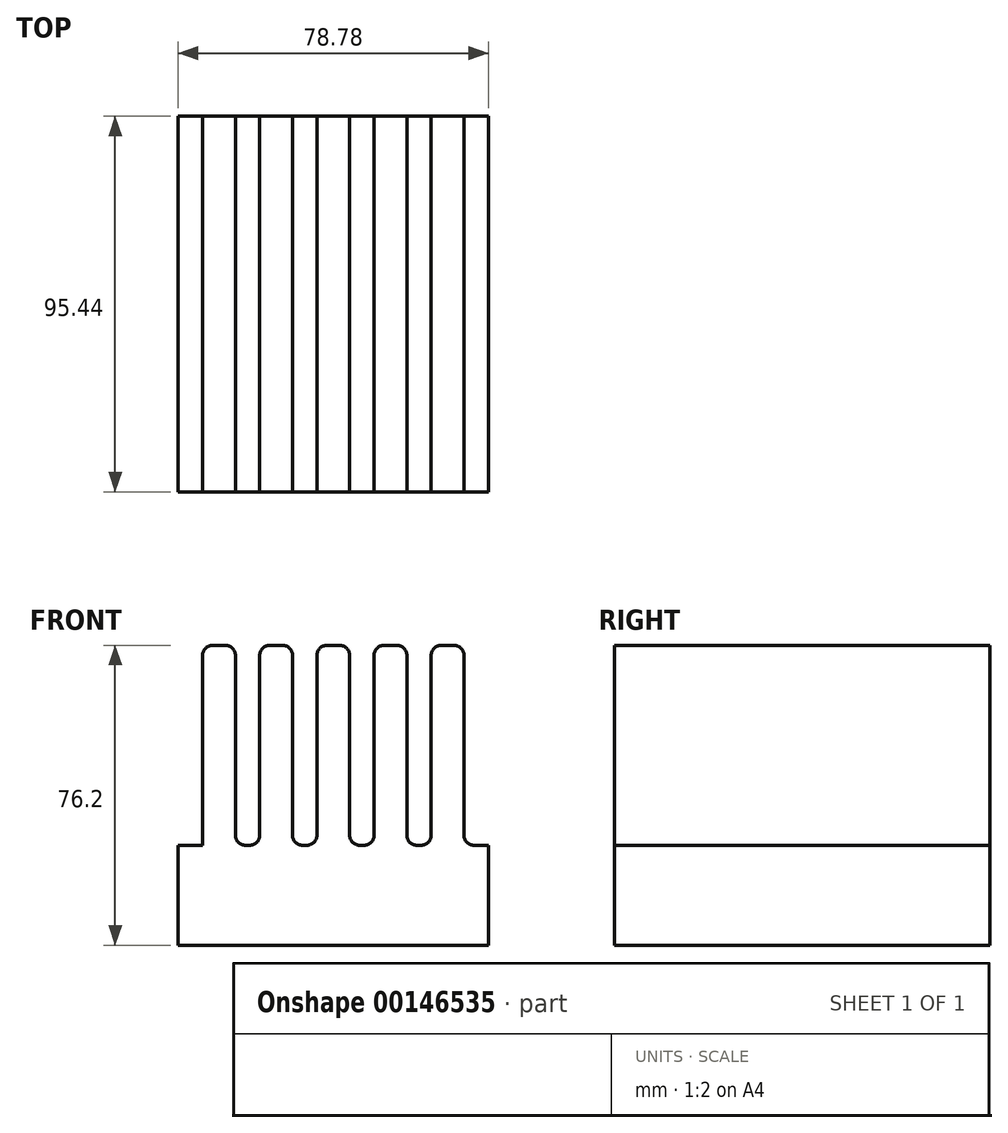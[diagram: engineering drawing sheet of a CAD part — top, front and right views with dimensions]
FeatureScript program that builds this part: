
annotation { "Feature Type Name" : "Feature", "Feature Type Description" : "" }
export const myFeature = defineFeature(function(context is Context, id is Id, definition is map)
    precondition{}
    {
        {
            var Q0;
            Q0=qCreatedBy(makeId("Top.planeOp"),FACE);
            var sketch = newSketch(context, id + "F0", { "sketchPlane" : qUnion([Q0])});
            skLineSegment(sketch, "E0.bottom", {"start": v(47.72, -47.72) * mm, "end": v(-47.72, -47.72) * mm});
            skLineSegment(sketch, "E0.top", {"start": v(47.72, 47.72) * mm, "end": v(-47.72, 47.72) * mm});
            skLineSegment(sketch, "E0.left", {"start": v(47.72, -47.72) * mm, "end": v(47.72, 47.72) * mm});
            skLineSegment(sketch, "E0.right", {"start": v(-47.72, -47.72) * mm, "end": v(-47.72, 47.72) * mm});
            skPoint(sketch, "E0.middle", {"position": v(0, 0) * mm});
            skLineSegment(sketch, "E1.bottom", {"start": v(-47.72, 47.72) * mm, "end": v(-39.39, 47.72) * mm});
            skLineSegment(sketch, "E1.top", {"start": v(-47.72, -47.72) * mm, "end": v(-39.39, -47.72) * mm});
            skLineSegment(sketch, "E1.left", {"start": v(-47.72, 47.72) * mm, "end": v(-47.72, -47.72) * mm});
            skLineSegment(sketch, "E1.right", {"start": v(-39.39, 47.72) * mm, "end": v(-39.39, -47.72) * mm});
            skLineSegment(sketch, "E2.1.0.0", {"start": v(-24.87, 47.72) * mm, "end": v(-24.87, -47.72) * mm});
            skLineSegment(sketch, "E2.1.0.1", {"start": v(-33.2, 47.72) * mm, "end": v(-24.87, 47.72) * mm});
            skLineSegment(sketch, "E2.1.0.2", {"start": v(-33.2, 47.72) * mm, "end": v(-33.2, -47.72) * mm});
            skLineSegment(sketch, "E2.1.0.3", {"start": v(-33.2, -47.72) * mm, "end": v(-24.87, -47.72) * mm});
            skLineSegment(sketch, "E2.2.0.0", {"start": v(-10.35, 47.72) * mm, "end": v(-10.35, -47.72) * mm});
            skLineSegment(sketch, "E2.2.0.1", {"start": v(-18.69, 47.72) * mm, "end": v(-10.35, 47.72) * mm});
            skLineSegment(sketch, "E2.2.0.2", {"start": v(-18.69, 47.72) * mm, "end": v(-18.69, -47.72) * mm});
            skLineSegment(sketch, "E2.2.0.3", {"start": v(-18.69, -47.72) * mm, "end": v(-10.35, -47.72) * mm});
            skLineSegment(sketch, "E2.3.0.0", {"start": v(4.17, 47.72) * mm, "end": v(4.17, -47.72) * mm});
            skLineSegment(sketch, "E2.3.0.1", {"start": v(-4.17, 47.72) * mm, "end": v(4.17, 47.72) * mm});
            skLineSegment(sketch, "E2.3.0.2", {"start": v(-4.17, 47.72) * mm, "end": v(-4.17, -47.72) * mm});
            skLineSegment(sketch, "E2.3.0.3", {"start": v(-4.17, -47.72) * mm, "end": v(4.17, -47.72) * mm});
            skLineSegment(sketch, "E2.4.0.0", {"start": v(18.69, 47.72) * mm, "end": v(18.69, -47.72) * mm});
            skLineSegment(sketch, "E2.4.0.1", {"start": v(10.35, 47.72) * mm, "end": v(18.69, 47.72) * mm});
            skLineSegment(sketch, "E2.4.0.2", {"start": v(10.35, 47.72) * mm, "end": v(10.35, -47.72) * mm});
            skLineSegment(sketch, "E2.4.0.3", {"start": v(10.35, -47.72) * mm, "end": v(18.69, -47.72) * mm});
            skLineSegment(sketch, "E2.5.0.0", {"start": v(33.2, 47.72) * mm, "end": v(33.2, -47.72) * mm});
            skLineSegment(sketch, "E2.5.0.1", {"start": v(24.87, 47.72) * mm, "end": v(33.2, 47.72) * mm});
            skLineSegment(sketch, "E2.5.0.2", {"start": v(24.87, 47.72) * mm, "end": v(24.87, -47.72) * mm});
            skLineSegment(sketch, "E2.5.0.3", {"start": v(24.87, -47.72) * mm, "end": v(33.2, -47.72) * mm});
            skLineSegment(sketch, "E2.6.0.0", {"start": v(47.72, 47.72) * mm, "end": v(47.72, -47.72) * mm});
            skLineSegment(sketch, "E2.6.0.1", {"start": v(39.39, 47.72) * mm, "end": v(47.72, 47.72) * mm});
            skLineSegment(sketch, "E2.6.0.2", {"start": v(39.39, 47.72) * mm, "end": v(39.39, -47.72) * mm});
            skLineSegment(sketch, "E2.6.0.3", {"start": v(39.39, -47.72) * mm, "end": v(47.72, -47.72) * mm});
            skLineSegment(sketch, "E2.direction1", {"start": v(-39.39, -47.72) * mm, "end": v(-24.87, -47.72) * mm, "construction": true});
            skSolve(sketch);
        }
        {
            var Q0;
            Q0=makeQuery(id+"F0.imprint","IMPRINT",FACE,{"disambiguationData":[TD([[makeQuery(id+"F0.imprint","IMPRINT",EDGE,{"derivedFrom":sQuery(id+"F0.wireOp",EDGE,"E1.bottom")}),-1.0]])]});
            var Q1;
            Q1=makeQuery(id+"F0.imprint","IMPRINT",FACE,{"disambiguationData":[TD([[makeQuery(id+"F0.imprint","IMPRINT",EDGE,{"derivedFrom":sQuery(id+"F0.wireOp",EDGE,"E2.6.0.0")}),-1.0]])]});
            var Q2;
            {var subQ2=sQuery(id+"F0.wireOp",EDGE,"E2.5.0.0");Q2=makeQuery(id+"F0.imprint","IMPRINT",FACE,{"disambiguationData":[TD([[makeQuery(id+"F0.imprint","IMPRINT",EDGE,{"derivedFrom":subQ2}),1.0]])]});}
            var Q3;
            {var subQ0=sQuery(id+"F0.wireOp",EDGE,"E2.4.0.0");Q3=makeQuery(id+"F0.imprint","IMPRINT",FACE,{"disambiguationData":[TD([[makeQuery(id+"F0.imprint","IMPRINT",EDGE,{"derivedFrom":subQ0}),1.0]])]});}
            var Q4;
            {var subQ0=sQuery(id+"F0.wireOp",EDGE,"E2.3.0.0");Q4=makeQuery(id+"F0.imprint","IMPRINT",FACE,{"disambiguationData":[TD([[makeQuery(id+"F0.imprint","IMPRINT",EDGE,{"derivedFrom":subQ0}),1.0]])]});}
            var Q5;
            {var subQ0=sQuery(id+"F0.wireOp",EDGE,"E2.2.0.0");Q5=makeQuery(id+"F0.imprint","IMPRINT",FACE,{"disambiguationData":[TD([[makeQuery(id+"F0.imprint","IMPRINT",EDGE,{"derivedFrom":subQ0}),1.0]])]});}
            var Q6;
            {var subQ0=sQuery(id+"F0.wireOp",EDGE,"E2.1.0.0");Q6=makeQuery(id+"F0.imprint","IMPRINT",FACE,{"disambiguationData":[TD([[makeQuery(id+"F0.imprint","IMPRINT",EDGE,{"derivedFrom":subQ0}),1.0]])]});}
            var Q7;
            {var subQ0=sQuery(id+"F0.wireOp",EDGE,"E1.right");Q7=makeQuery(id+"F0.imprint","IMPRINT",FACE,{"disambiguationData":[TD([[makeQuery(id+"F0.imprint","IMPRINT",EDGE,{"derivedFrom":subQ0}),1.0]])]});}
            var Q8;
            Q8=makeQuery(id+"F0.imprint","IMPRINT",FACE,{"disambiguationData":[TD([[makeQuery(id+"F0.imprint","IMPRINT",EDGE,{"derivedFrom":sQuery(id+"F0.wireOp",EDGE,"E2.1.0.0")}),-1.0]])]});
            var Q9;
            Q9=makeQuery(id+"F0.imprint","IMPRINT",FACE,{"disambiguationData":[TD([[makeQuery(id+"F0.imprint","IMPRINT",EDGE,{"derivedFrom":sQuery(id+"F0.wireOp",EDGE,"E2.2.0.0")}),-1.0]])]});
            var Q10;
            Q10=makeQuery(id+"F0.imprint","IMPRINT",FACE,{"disambiguationData":[TD([[makeQuery(id+"F0.imprint","IMPRINT",EDGE,{"derivedFrom":sQuery(id+"F0.wireOp",EDGE,"E2.3.0.0")}),-1.0]])]});
            var Q11;
            Q11=makeQuery(id+"F0.imprint","IMPRINT",FACE,{"disambiguationData":[TD([[makeQuery(id+"F0.imprint","IMPRINT",EDGE,{"derivedFrom":sQuery(id+"F0.wireOp",EDGE,"E2.4.0.0")}),-1.0]])]});
            var Q12;
            Q12=makeQuery(id+"F0.imprint","IMPRINT",FACE,{"disambiguationData":[TD([[makeQuery(id+"F0.imprint","IMPRINT",EDGE,{"derivedFrom":sQuery(id+"F0.wireOp",EDGE,"E2.5.0.0")}),-1.0]])]});
            extrude(context, id + "F1", {"entities" : qUnion([Q0, Q1, Q2, Q3, Q4, Q5, Q6, Q7, Q8, Q9, Q10, Q11, Q12]), "oppositeDirection" : true, "depth" : 25.4 * mm});
        }
        {
            var Q0;
            Q0=makeQuery(id+"F0.imprint","IMPRINT",FACE,{"disambiguationData":[TD([[makeQuery(id+"F0.imprint","IMPRINT",EDGE,{"derivedFrom":sQuery(id+"F0.wireOp",EDGE,"E1.bottom")}),-1.0]])]});
            var Q1;
            Q1=makeQuery(id+"F0.imprint","IMPRINT",FACE,{"disambiguationData":[TD([[makeQuery(id+"F0.imprint","IMPRINT",EDGE,{"derivedFrom":sQuery(id+"F0.wireOp",EDGE,"E2.1.0.0")}),-1.0]])]});
            var Q2;
            Q2=makeQuery(id+"F0.imprint","IMPRINT",FACE,{"disambiguationData":[TD([[makeQuery(id+"F0.imprint","IMPRINT",EDGE,{"derivedFrom":sQuery(id+"F0.wireOp",EDGE,"E2.2.0.0")}),-1.0]])]});
            var Q3;
            Q3=makeQuery(id+"F0.imprint","IMPRINT",FACE,{"disambiguationData":[TD([[makeQuery(id+"F0.imprint","IMPRINT",EDGE,{"derivedFrom":sQuery(id+"F0.wireOp",EDGE,"E2.3.0.0")}),-1.0]])]});
            var Q4;
            Q4=makeQuery(id+"F0.imprint","IMPRINT",FACE,{"disambiguationData":[TD([[makeQuery(id+"F0.imprint","IMPRINT",EDGE,{"derivedFrom":sQuery(id+"F0.wireOp",EDGE,"E2.4.0.0")}),-1.0]])]});
            var Q5;
            Q5=makeQuery(id+"F0.imprint","IMPRINT",FACE,{"disambiguationData":[TD([[makeQuery(id+"F0.imprint","IMPRINT",EDGE,{"derivedFrom":sQuery(id+"F0.wireOp",EDGE,"E2.5.0.0")}),-1.0]])]});
            var Q6;
            Q6=makeQuery(id+"F0.imprint","IMPRINT",FACE,{"disambiguationData":[TD([[makeQuery(id+"F0.imprint","IMPRINT",EDGE,{"derivedFrom":sQuery(id+"F0.wireOp",EDGE,"E2.6.0.0")}),-1.0]])]});
            extrude(context, id + "F2", {"entities" : qUnion([Q0, Q1, Q2, Q3, Q4, Q5, Q6]), "operationType" : NewBodyOperationType.ADD, "depth" : 50.8 * mm});
        }
        {
            var Q0;
            Q0=makeQuery(id+"F2.opExtrude","CAP_EDGE",EDGE,{"disambiguationData":[OSD([sQuery(id+"F0.wireOp",EDGE,"E1.left")])],"isStart":false});
            var Q1;
            Q1=makeQuery(id+"F2.opExtrude","CAP_EDGE",EDGE,{"disambiguationData":[OSD([sQuery(id+"F0.wireOp",EDGE,"E1.right")])],"isStart":false});
            var Q2;
            Q2=makeQuery(id+"F2.opExtrude","CAP_EDGE",EDGE,{"disambiguationData":[OSD([sQuery(id+"F0.wireOp",EDGE,"E2.1.0.2")])],"isStart":false});
            var Q3;
            Q3=makeQuery(id+"F2.opExtrude","CAP_EDGE",EDGE,{"disambiguationData":[OSD([sQuery(id+"F0.wireOp",EDGE,"E2.1.0.0")])],"isStart":false});
            var Q4;
            Q4=makeQuery(id+"F2.opExtrude","CAP_EDGE",EDGE,{"disambiguationData":[OSD([sQuery(id+"F0.wireOp",EDGE,"E2.2.0.2")])],"isStart":false});
            var Q5;
            Q5=makeQuery(id+"F2.opExtrude","CAP_EDGE",EDGE,{"disambiguationData":[OSD([sQuery(id+"F0.wireOp",EDGE,"E2.2.0.0")])],"isStart":false});
            var Q6;
            Q6=makeQuery(id+"F2.opExtrude","CAP_EDGE",EDGE,{"disambiguationData":[OSD([sQuery(id+"F0.wireOp",EDGE,"E2.3.0.2")])],"isStart":false});
            var Q7;
            Q7=makeQuery(id+"F2.opExtrude","CAP_EDGE",EDGE,{"disambiguationData":[OSD([sQuery(id+"F0.wireOp",EDGE,"E2.3.0.0")])],"isStart":false});
            var Q8;
            Q8=makeQuery(id+"F2.opExtrude","CAP_EDGE",EDGE,{"disambiguationData":[OSD([sQuery(id+"F0.wireOp",EDGE,"E2.4.0.2")])],"isStart":false});
            var Q9;
            Q9=makeQuery(id+"F2.opExtrude","CAP_EDGE",EDGE,{"disambiguationData":[OSD([sQuery(id+"F0.wireOp",EDGE,"E2.4.0.0")])],"isStart":false});
            var Q10;
            Q10=makeQuery(id+"F2.opExtrude","CAP_EDGE",EDGE,{"disambiguationData":[OSD([sQuery(id+"F0.wireOp",EDGE,"E2.5.0.2")])],"isStart":false});
            var Q11;
            Q11=makeQuery(id+"F2.opExtrude","CAP_EDGE",EDGE,{"disambiguationData":[OSD([sQuery(id+"F0.wireOp",EDGE,"E2.5.0.0")])],"isStart":false});
            var Q12;
            Q12=makeQuery(id+"F2.opExtrude","CAP_EDGE",EDGE,{"disambiguationData":[OSD([sQuery(id+"F0.wireOp",EDGE,"E2.6.0.2")])],"isStart":false});
            var Q13;
            Q13=makeQuery(id+"F2.opExtrude","CAP_EDGE",EDGE,{"disambiguationData":[OSD([sQuery(id+"F0.wireOp",EDGE,"E2.6.0.0")])],"isStart":false});
            var Q14;
            Q14=makeQuery(id+"F2.opExtrude","CAP_EDGE",EDGE,{"disambiguationData":[OSD([sQuery(id+"F0.wireOp",EDGE,"E2.5.0.0")])],"isStart":true});
            var Q15;
            Q15=makeQuery(id+"F2.opExtrude","CAP_EDGE",EDGE,{"disambiguationData":[OSD([sQuery(id+"F0.wireOp",EDGE,"E2.4.0.0")])],"isStart":true});
            var Q16;
            Q16=makeQuery(id+"F2.opExtrude","CAP_EDGE",EDGE,{"disambiguationData":[OSD([sQuery(id+"F0.wireOp",EDGE,"E2.3.0.0")])],"isStart":true});
            var Q17;
            Q17=makeQuery(id+"F2.opExtrude","CAP_EDGE",EDGE,{"disambiguationData":[OSD([sQuery(id+"F0.wireOp",EDGE,"E2.2.0.0")])],"isStart":true});
            var Q18;
            Q18=makeQuery(id+"F2.opExtrude","CAP_EDGE",EDGE,{"disambiguationData":[OSD([sQuery(id+"F0.wireOp",EDGE,"E2.1.0.0")])],"isStart":true});
            var Q19;
            Q19=makeQuery(id+"F2.opExtrude","CAP_EDGE",EDGE,{"disambiguationData":[OSD([sQuery(id+"F0.wireOp",EDGE,"E1.right")])],"isStart":true});
            var Q20;
            Q20=makeQuery(id+"F2.opExtrude","CAP_EDGE",EDGE,{"disambiguationData":[OSD([sQuery(id+"F0.wireOp",EDGE,"E2.1.0.2")])],"isStart":true});
            var Q21;
            Q21=makeQuery(id+"F2.opExtrude","CAP_EDGE",EDGE,{"disambiguationData":[OSD([sQuery(id+"F0.wireOp",EDGE,"E2.2.0.2")])],"isStart":true});
            var Q22;
            Q22=makeQuery(id+"F2.opExtrude","CAP_EDGE",EDGE,{"disambiguationData":[OSD([sQuery(id+"F0.wireOp",EDGE,"E2.3.0.2")])],"isStart":true});
            var Q23;
            Q23=makeQuery(id+"F2.opExtrude","CAP_EDGE",EDGE,{"disambiguationData":[OSD([sQuery(id+"F0.wireOp",EDGE,"E2.4.0.2")])],"isStart":true});
            var Q24;
            Q24=makeQuery(id+"F2.opExtrude","CAP_EDGE",EDGE,{"disambiguationData":[OSD([sQuery(id+"F0.wireOp",EDGE,"E2.5.0.2")])],"isStart":true});
            var Q25;
            Q25=makeQuery(id+"F2.opExtrude","CAP_EDGE",EDGE,{"disambiguationData":[OSD([sQuery(id+"F0.wireOp",EDGE,"E2.6.0.2")])],"isStart":true});
            fillet(context, id + "F3", {"entities" : qUnion([Q0, Q1, Q2, Q3, Q4, Q5, Q6, Q7, Q8, Q9, Q10, Q11, Q12, Q13, Q14, Q15, Q16, Q17, Q18, Q19, Q20, Q21, Q22, Q23, Q24, Q25]), "radius" : 2.54 * mm, "tangentPropagation" : true, "allowEdgeOverflow" : false});
        }
    });
